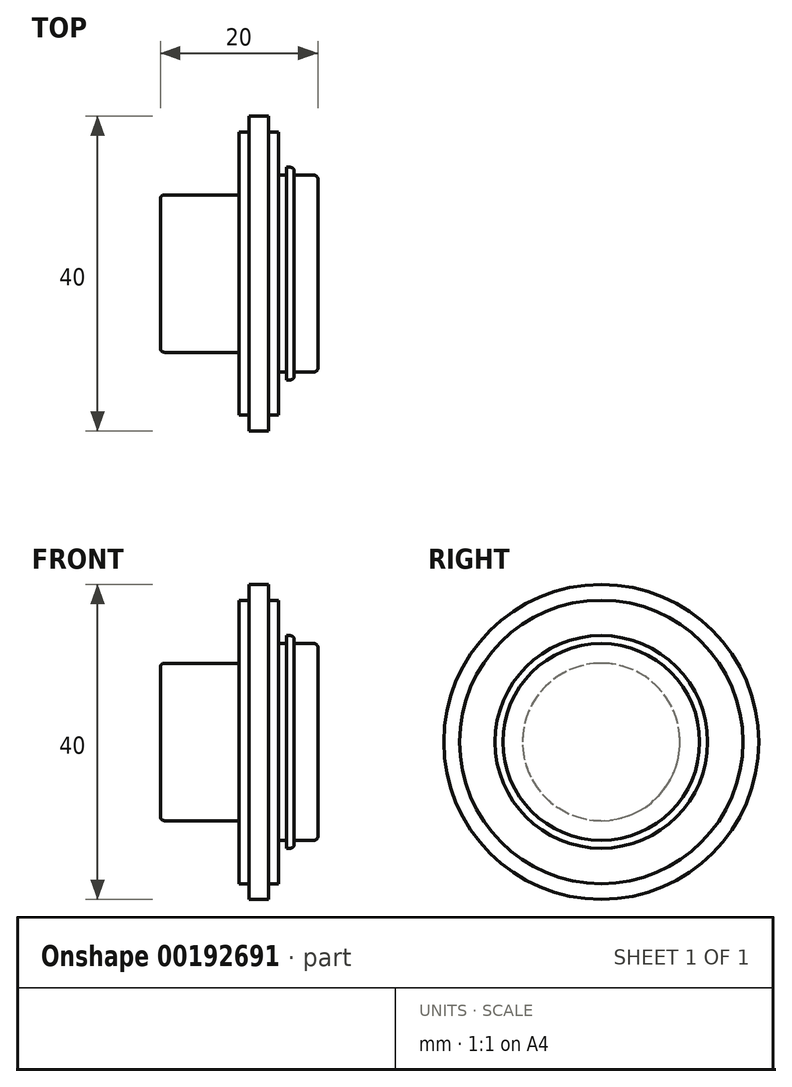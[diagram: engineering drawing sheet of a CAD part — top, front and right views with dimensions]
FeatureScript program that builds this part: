
annotation { "Feature Type Name" : "Feature", "Feature Type Description" : "" }
export const myFeature = defineFeature(function(context is Context, id is Id, definition is map)
    precondition{}
    {
        {
            var Q0;
            Q0=qCreatedBy(makeId("Front.planeOp"),FACE);
            var sketch = newSketch(context, id + "F0", { "sketchPlane" : qUnion([Q0])});
            skLineSegment(sketch, "E0", {"start": v(0, 0) * mm, "end": v(0, 12.5) * mm});
            skLineSegment(sketch, "E1", {"start": v(0, 12.5) * mm, "end": v(-3, 12.5) * mm});
            skLineSegment(sketch, "E2", {"start": v(-3, 12.5) * mm, "end": v(-3, 13.5) * mm});
            skLineSegment(sketch, "E3", {"start": v(-3, 13.5) * mm, "end": v(-4, 13.5) * mm});
            skLineSegment(sketch, "E4", {"start": v(-4, 13.5) * mm, "end": v(-4, 12.5) * mm});
            skLineSegment(sketch, "E5", {"start": v(-4, 12.5) * mm, "end": v(-5, 12.5) * mm});
            skLineSegment(sketch, "E6", {"start": v(-5, 12.5) * mm, "end": v(-5, 18) * mm});
            skLineSegment(sketch, "E7", {"start": v(-5, 18) * mm, "end": v(-6.25, 18) * mm});
            skLineSegment(sketch, "E8", {"start": v(-6.25, 18) * mm, "end": v(-6.25, 20) * mm});
            skLineSegment(sketch, "E9", {"start": v(-6.25, 20) * mm, "end": v(-8.75, 20) * mm});
            skLineSegment(sketch, "E10", {"start": v(-8.75, 20) * mm, "end": v(-8.75, 18) * mm});
            skLineSegment(sketch, "E11", {"start": v(-8.75, 18) * mm, "end": v(-10, 18) * mm});
            skLineSegment(sketch, "E12", {"start": v(0, 0) * mm, "end": v(-20, 0) * mm});
            skLineSegment(sketch, "E13", {"start": v(-10, 18) * mm, "end": v(-10, 10) * mm});
            skLineSegment(sketch, "E14", {"start": v(-20, 10) * mm, "end": v(-10, 10) * mm});
            skLineSegment(sketch, "E15", {"start": v(-20, 10) * mm, "end": v(-20, 0) * mm});
            skSolve(sketch);
        }
        {
            var Q0;
            Q0 = qSketchRegion(id + "F0", true);
            var Q1;
            Q1=sQuery(id+"F0.wireOp",EDGE,"E12");
            revolve(context, id + "F1", {"entities" : qUnion([Q0]), "axis" : qUnion([Q1]), "revolveType" : RevolveType.FULL});
        }
        {
            var Q0;
            Q0=makeQuery(id+"F1.opRevolve","SWEPT_EDGE",EDGE,{"disambiguationData":[OSD([sQuery(id+"F0.wireOp",EDGE,"E14"),sQuery(id+"F0.wireOp",EDGE,"E15")])]});
            var Q1;
            Q1=makeQuery(id+"F1.opRevolve","SWEPT_EDGE",EDGE,{"disambiguationData":[OSD([sQuery(id+"F0.wireOp",EDGE,"E2"),sQuery(id+"F0.wireOp",EDGE,"E3")])]});
            var Q2;
            Q2=makeQuery(id+"F1.opRevolve","SWEPT_EDGE",EDGE,{"disambiguationData":[OSD([sQuery(id+"F0.wireOp",EDGE,"E0"),sQuery(id+"F0.wireOp",EDGE,"E1")])]});
            fillet(context, id + "F2", {"entities" : qUnion([Q0, Q1, Q2]), "radius" : 0.5 * mm, "tangentPropagation" : true, "allowEdgeOverflow" : false});
        }
    });
